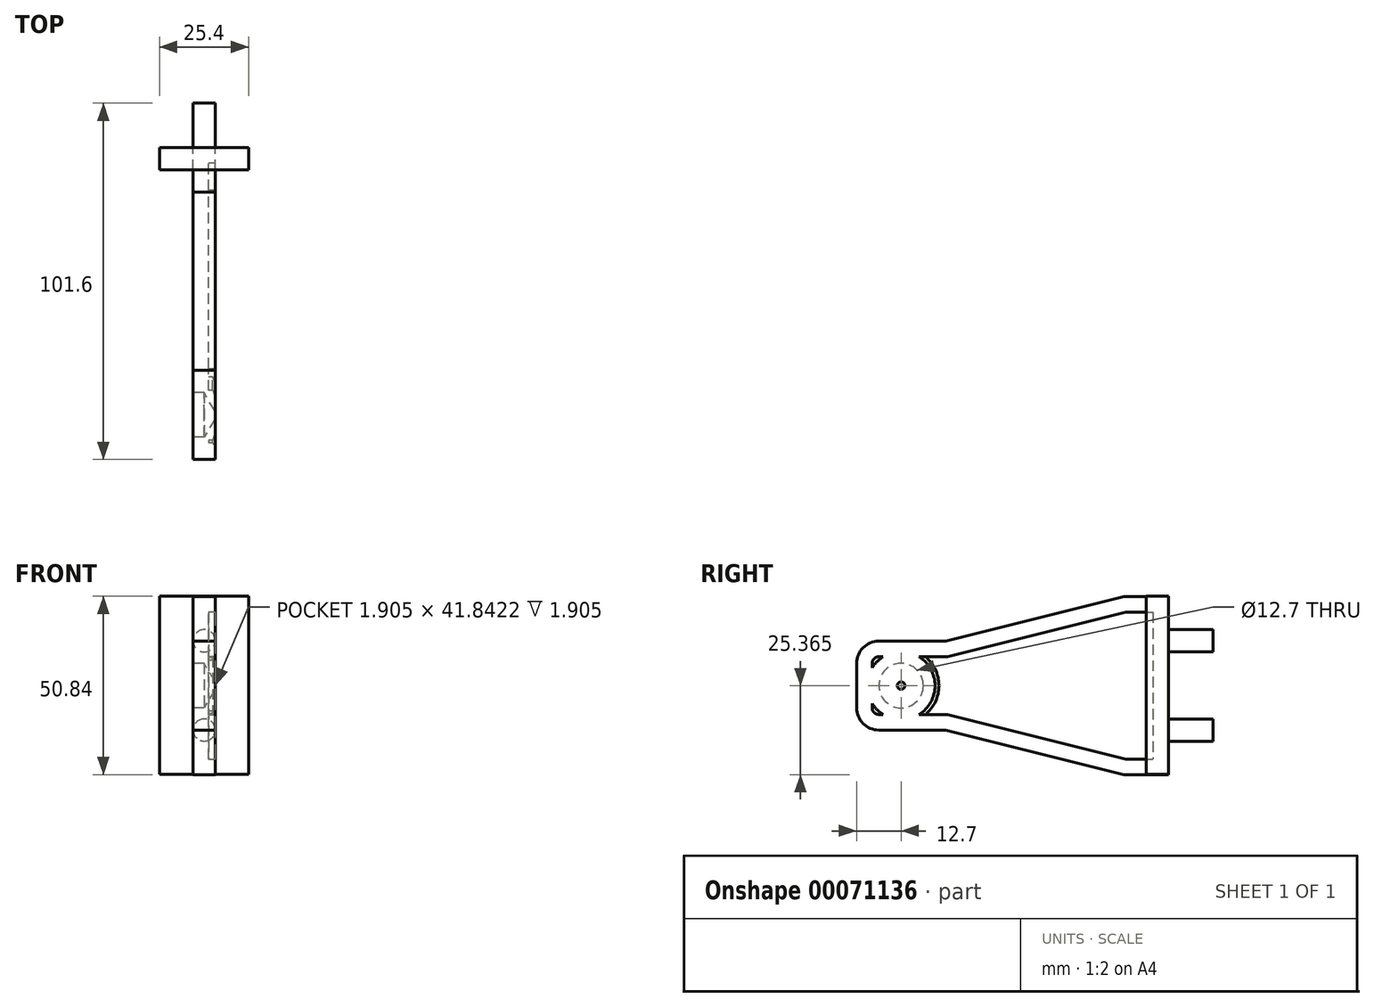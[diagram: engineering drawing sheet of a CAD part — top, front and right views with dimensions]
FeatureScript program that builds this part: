
annotation { "Feature Type Name" : "Feature", "Feature Type Description" : "" }
export const myFeature = defineFeature(function(context is Context, id is Id, definition is map)
    precondition{}
    {
        {
            var Q0;
            Q0=qCreatedBy(makeId("Front.planeOp"),FACE);
            var sketch = newSketch(context, id + "F0", { "sketchPlane" : qUnion([Q0])});
            skLineSegment(sketch, "E0.bottom", {"start": v(-33.9, -11.69) * mm, "end": v(-8.5, -11.69) * mm});
            skLineSegment(sketch, "E0.top", {"start": v(-33.9, 39.11) * mm, "end": v(-8.5, 39.11) * mm});
            skLineSegment(sketch, "E0.left", {"start": v(-33.9, -11.69) * mm, "end": v(-33.9, 39.11) * mm});
            skLineSegment(sketch, "E0.right", {"start": v(-8.5, -11.69) * mm, "end": v(-8.5, 39.11) * mm});
            skSolve(sketch);
        }
        {
            var Q0;
            Q0 = qSketchRegion(id + "F0", true);
            extrude(context, id + "F1", {"entities" : qUnion([Q0]), "depth" : 6.35 * mm});
        }
        {
            var Q0;
            Q0=qCreatedBy(makeId("Front.planeOp"),FACE);
            var sketch = newSketch(context, id + "F2", { "sketchPlane" : qUnion([Q0])});
            skLineSegment(sketch, "E1.bottom", {"start": v(-24.38, 39) * mm, "end": v(-18.03, 39) * mm});
            skLineSegment(sketch, "E1.top", {"start": v(-24.38, -11.73) * mm, "end": v(-18.03, -11.73) * mm});
            skLineSegment(sketch, "E1.left", {"start": v(-24.38, 39) * mm, "end": v(-24.38, -11.73) * mm});
            skLineSegment(sketch, "E1.right", {"start": v(-18.03, 39) * mm, "end": v(-18.03, -11.73) * mm});
            skSolve(sketch);
        }
        {
            var Q0;
            Q0 = qSketchRegion(id + "F2", true);
            extrude(context, id + "F3", {"entities" : qUnion([Q0]), "operationType" : NewBodyOperationType.ADD, "depth" : 12.7 * mm});
        }
        {
            var Q0;
            Q0=makeQuery(id+"F3.opExtrude","CAP_FACE",FACE,{"disambiguationData":[OSD([sQuery(id+"F2.wireOp",EDGE,"E1.bottom"),sQuery(id+"F2.wireOp",EDGE,"E1.top"),sQuery(id+"F2.wireOp",EDGE,"E1.left"),sQuery(id+"F2.wireOp",EDGE,"E1.right")])],"isStart":false});
            cPlane(context, id + "F4", {"entities" : qUnion([Q0]), "cplaneType" : CPlaneType.OFFSET, "offset" : 50.8 * mm, "width" : 152.4 * mm, "height" : 152.4 * mm});
        }
        {
            var Q0;
            Q0=qCreatedBy(id+"F4.planeOp",FACE);
            var sketch = newSketch(context, id + "F5", { "sketchPlane" : qUnion([Q0])});
            skLineSegment(sketch, "E2.0", {"start": v(-24.38, 26.3) * mm, "end": v(-24.38, 0.97) * mm});
            skLineSegment(sketch, "E3.0", {"start": v(-18.03, 26.3) * mm, "end": v(-18.03, 0.97) * mm});
            skLineSegment(sketch, "E4", {"start": v(-24.38, 26.3) * mm, "end": v(-18.03, 26.3) * mm});
            skLineSegment(sketch, "E5", {"start": v(-24.38, 0.97) * mm, "end": v(-18.03, 0.97) * mm});
            skSolve(sketch);
        }
        {
            var Q1;
            Q1=makeQuery(id+"F3.opExtrude","CAP_FACE",FACE,{"disambiguationData":[OSD([sQuery(id+"F2.wireOp",EDGE,"E1.bottom"),sQuery(id+"F2.wireOp",EDGE,"E1.top"),sQuery(id+"F2.wireOp",EDGE,"E1.left"),sQuery(id+"F2.wireOp",EDGE,"E1.right")])],"isStart":false});
            var Q2;
            Q2=makeQuery(id+"F5.imprint","IMPRINT",FACE,{"disambiguationData":[TD([[makeQuery(id+"F5.imprint","IMPRINT",EDGE,{"derivedFrom":sQuery(id+"F5.wireOp",EDGE,"E2.0")}),1.0]])]});
            loft(context, id + "F6", {"operationType" : NewBodyOperationType.ADD, "sheetProfilesArray" : [{ "sheetProfileEntities" : qUnion([Q1]) }, { "sheetProfileEntities" : qUnion([Q2]) }]});
        }
        {
            var Q0;
            Q0=makeQuery(id+"F6.opLoft","CAP_FACE",FACE,{"disambiguationData":[OSD([makeQuery(id+"F5.imprint","IMPRINT",FACE,{"disambiguationData":[TD([[makeQuery(id+"F5.imprint","IMPRINT",EDGE,{"derivedFrom":sQuery(id+"F5.wireOp",EDGE,"E2.0")}),1.0]])]})])],"isStart":true});
            extrude(context, id + "F7", {"entities" : qUnion([Q0]), "operationType" : NewBodyOperationType.ADD, "depth" : 25.4 * mm});
        }
        {
            var Q0;
            Q0=makeQuery(id+"F7.opExtrude","CAP_EDGE",EDGE,{"disambiguationData":[OSD([sQuery(id+"F5.wireOp",EDGE,"E2.0"),sQuery(id+"F5.wireOp",EDGE,"E3.0"),sQuery(id+"F5.wireOp",EDGE,"E5")])],"isStart":false});
            var Q1;
            Q1=makeQuery(id+"F7.opExtrude","CAP_EDGE",EDGE,{"disambiguationData":[OSD([sQuery(id+"F5.wireOp",EDGE,"E2.0"),sQuery(id+"F5.wireOp",EDGE,"E3.0"),sQuery(id+"F5.wireOp",EDGE,"E4")])],"isStart":false});
            fillet(context, id + "F8", {"entities" : qUnion([Q0, Q1]), "radius" : 6.35 * mm, "tangentPropagation" : true, "allowEdgeOverflow" : false});
        }
        {
            var Q0;
            {var subQ0=sQuery(id+"F5.wireOp",EDGE,"E5");var subQ1=sQuery(id+"F5.wireOp",EDGE,"E4");var subQ2=sQuery(id+"F5.wireOp",EDGE,"E2.0");var subQ3=sQuery(id+"F2.wireOp",EDGE,"E1.left");Q0=makeQuery(id+"F7.boolean.opBoolean","MERGE",FACE,{"derivedFrom":[makeQuery(id+"F6.boolean.opBoolean","MERGE",FACE,{"derivedFrom":[makeQuery(id+"F3.opExtrude","SWEPT_FACE",FACE,{"disambiguationData":[OSD([subQ3])]}),makeQuery(id+"F6.opLoft","SWEPT_FACE",FACE,{"disambiguationData":[OSD([sQuery(id+"F2.wireOp",EDGE,"E1.bottom"),sQuery(id+"F2.wireOp",EDGE,"E1.top"),subQ3,subQ2,subQ1,subQ0])]})]}),makeQuery(id+"F7.opExtrude","SWEPT_FACE",FACE,{"disambiguationData":[OSD([subQ2,subQ1,subQ0])]})]});}
            var sketch = newSketch(context, id + "F9", { "sketchPlane" : qUnion([Q0])});
            skPoint(sketch, "E6", {"position": v(76.2, 13.63) * mm});
            skPoint(sketch, "E6.positionSnap0", {"position": v(88.9, 13.63) * mm});
            skSolve(sketch);
        }
        {
            var Q0;
            Q0=sQuery(id+"F9.wireOp",VERTEX,"E6");
            var Q1;
            Q1=makeQuery(id+"F1.opExtrude","SWEPT_BODY",BODY,{"disambiguationData":[OSD([sQuery(id+"F0.wireOp",EDGE,"E0.bottom"),sQuery(id+"F0.wireOp",EDGE,"E0.top"),sQuery(id+"F0.wireOp",EDGE,"E0.left"),sQuery(id+"F0.wireOp",EDGE,"E0.right")])]});
            hole(context, id + "F10", {"style" : HoleStyle.SIMPLE, "holeDiameter" : 12.7 * mm, "endStyle" : HoleEndStyle.BLIND, "holeDepth" : 3.17 * mm, "locations" : qUnion([Q0]), "scope" : qUnion([Q1])});
        }
        {
            var Q0;
            Q0=makeQuery(id+"F3.boolean.opBoolean","MERGE",FACE,{"derivedFrom":[makeQuery(id+"F1.opExtrude","CAP_FACE",FACE,{"disambiguationData":[OSD([sQuery(id+"F0.wireOp",EDGE,"E0.bottom"),sQuery(id+"F0.wireOp",EDGE,"E0.top"),sQuery(id+"F0.wireOp",EDGE,"E0.left"),sQuery(id+"F0.wireOp",EDGE,"E0.right")])],"isStart":true}),makeQuery(id+"F3.opExtrude","CAP_FACE",FACE,{"disambiguationData":[OSD([sQuery(id+"F2.wireOp",EDGE,"E1.bottom"),sQuery(id+"F2.wireOp",EDGE,"E1.top"),sQuery(id+"F2.wireOp",EDGE,"E1.left"),sQuery(id+"F2.wireOp",EDGE,"E1.right")])],"isStart":true})]});
            var sketch = newSketch(context, id + "F11", { "sketchPlane" : qUnion([Q0])});
            skCircle(sketch, "E7", {"center": v(21.13, 26.41) * mm, "radius": 3.18 * mm});
            skCircle(sketch, "E8", {"center": v(21.13, 0.97) * mm, "radius": 3.18 * mm});
            skSolve(sketch);
        }
        {
            var Q0;
            Q0=makeQuery(id+"F11.imprint","IMPRINT",FACE,{"disambiguationData":[TD([[makeQuery(id+"F11.imprint","IMPRINT",EDGE,{"derivedFrom":sQuery(id+"F11.wireOp",EDGE,"E7")}),1.0]])]});
            var Q1;
            Q1=makeQuery(id+"F11.imprint","IMPRINT",FACE,{"disambiguationData":[TD([[makeQuery(id+"F11.imprint","IMPRINT",EDGE,{"derivedFrom":sQuery(id+"F11.wireOp",EDGE,"E8")}),1.0]])]});
            extrude(context, id + "F12", {"entities" : qUnion([Q0, Q1]), "operationType" : NewBodyOperationType.ADD, "depth" : 12.7 * mm});
        }
        {
            var Q0;
            {var subQ0=sQuery(id+"F5.wireOp",EDGE,"E5");var subQ1=sQuery(id+"F5.wireOp",EDGE,"E4");var subQ2=sQuery(id+"F5.wireOp",EDGE,"E3.0");var subQ3=sQuery(id+"F2.wireOp",EDGE,"E1.right");Q0=makeQuery(id+"F7.boolean.opBoolean","MERGE",FACE,{"derivedFrom":[makeQuery(id+"F6.boolean.opBoolean","MERGE",FACE,{"derivedFrom":[makeQuery(id+"F3.opExtrude","SWEPT_FACE",FACE,{"disambiguationData":[OSD([subQ3])]}),makeQuery(id+"F6.opLoft","SWEPT_FACE",FACE,{"disambiguationData":[OSD([sQuery(id+"F2.wireOp",EDGE,"E1.bottom"),sQuery(id+"F2.wireOp",EDGE,"E1.top"),subQ3,subQ2,subQ1,subQ0])]})]}),makeQuery(id+"F7.opExtrude","SWEPT_FACE",FACE,{"disambiguationData":[OSD([subQ2,subQ1,subQ0])]})]});}
            shell(context, id + "F13", {"entities" : qUnion([Q0]), "thickness" : 4.44 * mm});
        }
    });
